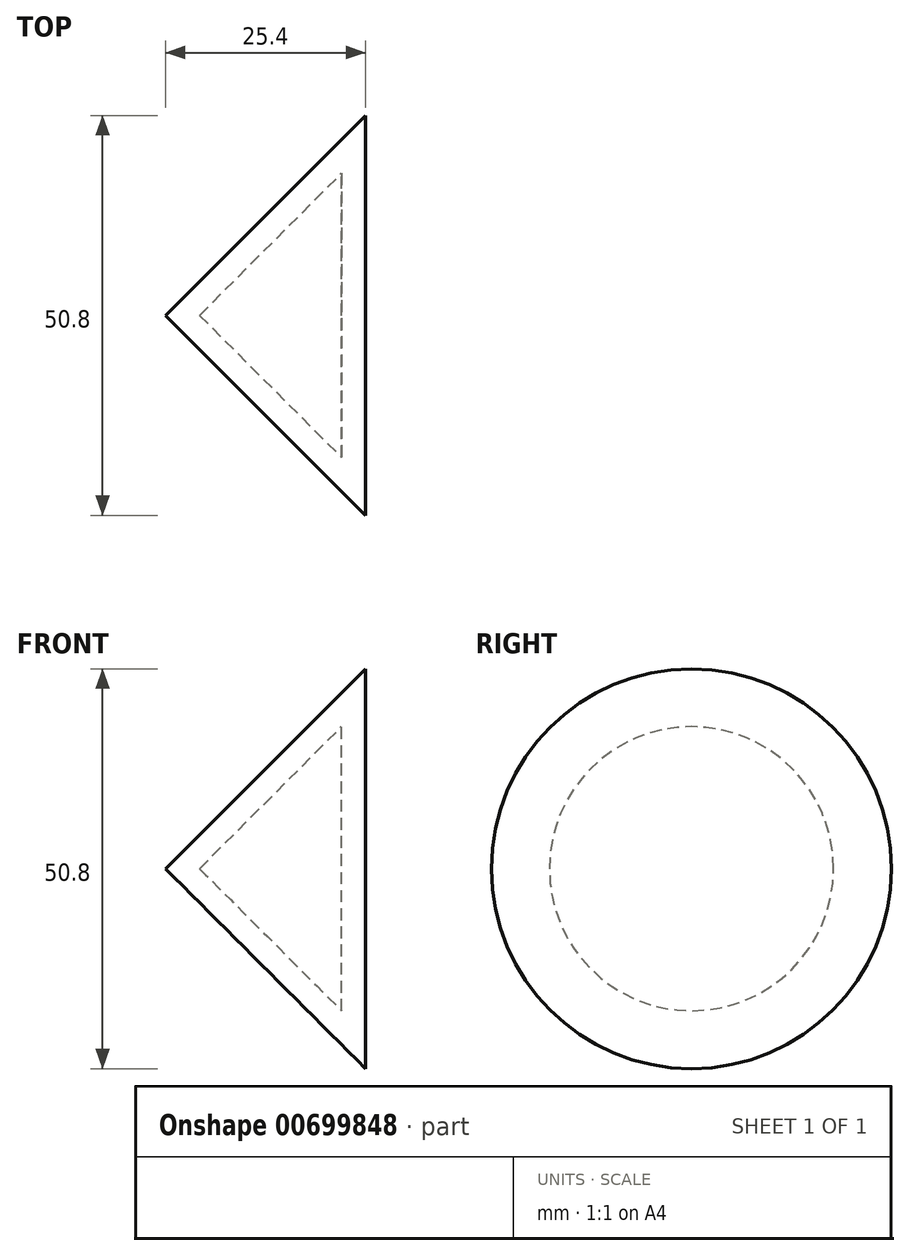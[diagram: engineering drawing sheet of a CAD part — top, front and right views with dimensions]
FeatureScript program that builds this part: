
annotation { "Feature Type Name" : "Feature", "Feature Type Description" : "" }
export const myFeature = defineFeature(function(context is Context, id is Id, definition is map)
    precondition{}
    {
        {
            var Q0;
            Q0=qCreatedBy(makeId("Front.planeOp"),FACE);
            var sketch = newSketch(context, id + "F0", { "sketchPlane" : qUnion([Q0])});
            skLineSegment(sketch, "E0", {"start": v(0, 0) * mm, "end": v(25.4, 25.4) * mm});
            skArc(sketch, "E1", {"start": v(0, 0) * mm, "mid": v(17.96, 7.44) * mm, "end": v(25.4, 25.4) * mm});
            skPoint(sketch, "E2", {"position": v(25.4, 25.4) * mm});
            skPoint(sketch, "E3", {"position": v(0, 0) * mm});
            skPoint(sketch, "E4.end.orphan", {"position": v(23.46, 0) * mm});
            skPoint(sketch, "E5.end.orphan", {"position": v(25.4, 0) * mm});
            skLineSegment(sketch, "E6", {"start": v(25.4, 0) * mm, "end": v(25.4, 25.4) * mm});
            skLineSegment(sketch, "E7", {"start": v(25.4, 0) * mm, "end": v(0, 0) * mm});
            skSolve(sketch);
        }
        {
            var Q0;
            Q0=makeQuery(id+"F0.imprint","IMPRINT",FACE,{"disambiguationData":[TD([[makeQuery(id+"F0.imprint","IMPRINT",EDGE,{"derivedFrom":sQuery(id+"F0.wireOp",EDGE,"E0")}),-1.0]])]});
            var Q1;
            Q1=makeQuery(id+"F0.imprint","IMPRINT",FACE,{"disambiguationData":[TD([[makeQuery(id+"F0.imprint","IMPRINT",EDGE,{"derivedFrom":sQuery(id+"F0.wireOp",EDGE,"E1")}),-1.0]])]});
            var Q2;
            Q2=sQuery(id+"F0.wireOp",EDGE,"E7");
            revolve(context, id + "F1", {"entities" : qUnion([Q0, Q1]), "axis" : qUnion([Q2]), "revolveType" : RevolveType.FULL});
        }
        {
            var Q0;
            Q0=makeQuery(id+"F1.opRevolve","SWEPT_FACE",FACE,{"disambiguationData":[OSD([sQuery(id+"F0.wireOp",EDGE,"E6")])]});
            var Q1;
            Q1=makeQuery(id+"F1.opRevolve","SWEPT_BODY",BODY,{"disambiguationData":[OSD([sQuery(id+"F0.wireOp",EDGE,"E0"),sQuery(id+"F0.wireOp",EDGE,"E6"),sQuery(id+"F0.wireOp",EDGE,"E7")])]});
            shell(context, id + "F2", {"isHollow" : true, "entities" : qUnion([Q0]), "parts" : qUnion([Q1]), "thickness" : 3.05 * mm});
        }
    });
